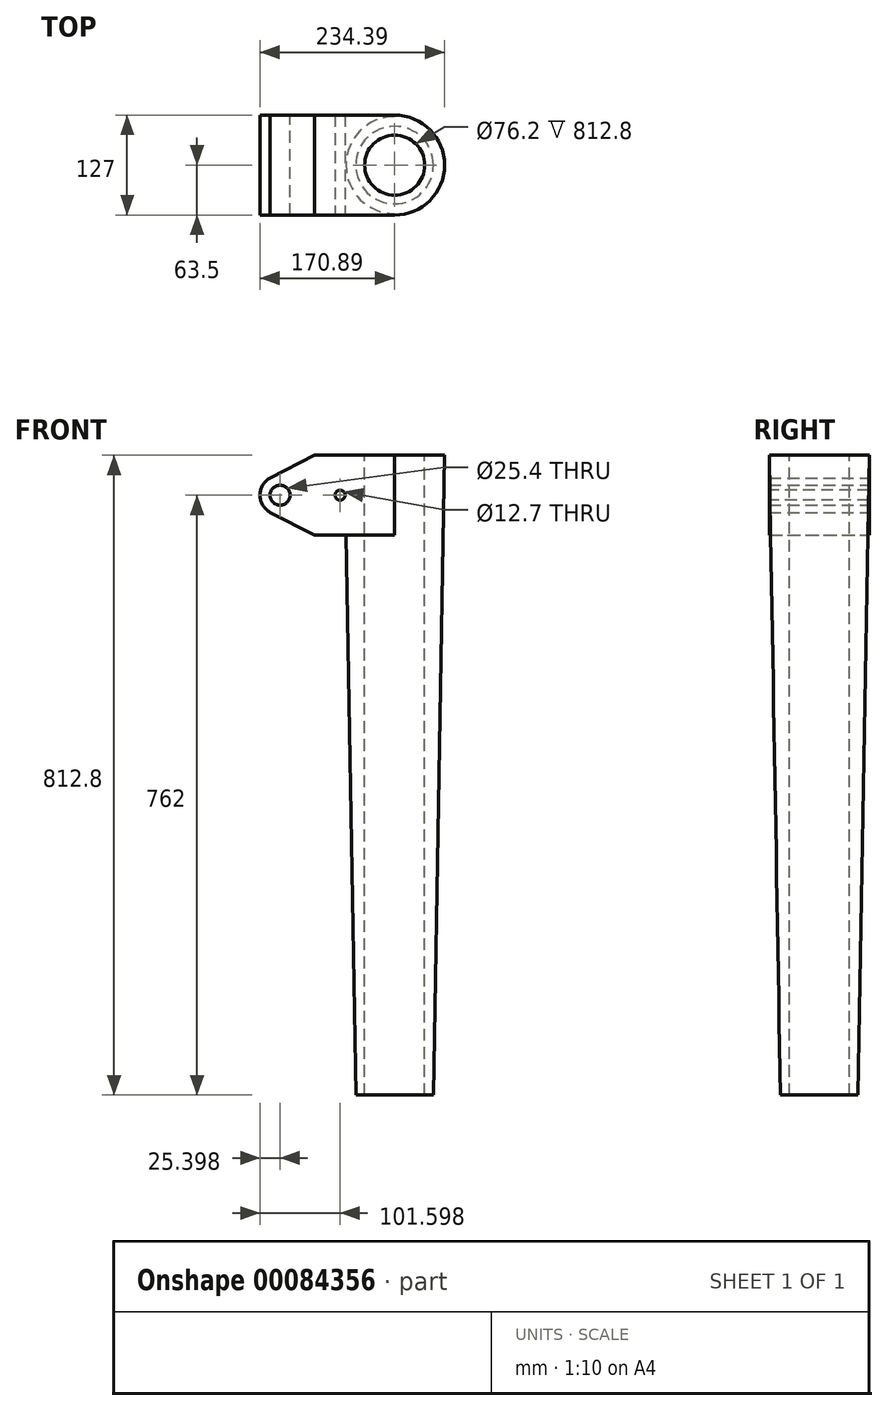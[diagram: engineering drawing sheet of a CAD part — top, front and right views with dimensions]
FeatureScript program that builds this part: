
annotation { "Feature Type Name" : "Feature", "Feature Type Description" : "" }
export const myFeature = defineFeature(function(context is Context, id is Id, definition is map)
    precondition{}
    {
        {
            var Q0;
            Q0=qCreatedBy(makeId("Front.planeOp"),FACE);
            var sketch = newSketch(context, id + "F0", { "sketchPlane" : qUnion([Q0])});
            skLineSegment(sketch, "E0.bottom", {"start": v(0, 0) * mm, "end": v(-101.6, 0) * mm});
            skLineSegment(sketch, "E0.top", {"start": v(0, 101.6) * mm, "end": v(-101.6, 101.6) * mm});
            skLineSegment(sketch, "E0.left", {"start": v(0, 0) * mm, "end": v(0, 101.6) * mm});
            skLineSegment(sketch, "E0.right", {"start": v(-101.6, 0) * mm, "end": v(-101.6, 101.6) * mm});
            skCircle(sketch, "E1", {"center": v(-145.5, 50.8) * mm, "radius": 12.7 * mm});
            skLineSegment(sketch, "E2", {"start": v(0, 50.8) * mm, "end": v(-213.64, 50.8) * mm, "construction": true});
            skArc(sketch, "E3", {"start": v(-158.2, 72.8) * mm, "mid": v(-170.9, 50.8) * mm, "end": v(-158.2, 28.8) * mm});
            skLineSegment(sketch, "E4", {"start": v(-158.2, 72.8) * mm, "end": v(-101.6, 101.6) * mm});
            skLineSegment(sketch, "E5", {"start": v(-158.2, 28.8) * mm, "end": v(-101.6, 0) * mm});
            skLineSegment(sketch, "E6", {"start": v(-158.2, 72.8) * mm, "end": v(-158.2, 28.8) * mm, "construction": true});
            skSolve(sketch);
        }
        {
            var Q0;
            Q0=makeQuery(id+"F0.imprint","IMPRINT",FACE,{"disambiguationData":[TD([[makeQuery(id+"F0.imprint","IMPRINT",EDGE,{"derivedFrom":sQuery(id+"F0.wireOp",EDGE,"E0.bottom")}),-1.0]])]});
            var Q1;
            Q1=makeQuery(id+"F0.imprint","IMPRINT",FACE,{"disambiguationData":[TD([[makeQuery(id+"F0.imprint","IMPRINT",EDGE,{"derivedFrom":sQuery(id+"F0.wireOp",EDGE,"E0.right")}),1.0]])]});
            extrude(context, id + "F1", {"entities" : qUnion([Q0, Q1]), "endBound" : BoundingType.SYMMETRIC, "depth" : 127 * mm});
        }
        {
            var Q0;
            Q0=makeQuery(id+"F1.opExtrude","SWEPT_FACE",FACE,{"disambiguationData":[OSD([sQuery(id+"F0.wireOp",EDGE,"E0.top")])]});
            var sketch = newSketch(context, id + "F2", { "sketchPlane" : qUnion([Q0])});
            skLineSegment(sketch, "E7.0", {"start": v(0, -63.5) * mm, "end": v(0, 63.5) * mm});
            skLineSegment(sketch, "E7.1", {"start": v(0, 63.5) * mm, "end": v(-101.6, 63.5) * mm});
            skLineSegment(sketch, "E7.2", {"start": v(0, -63.5) * mm, "end": v(-101.6, -63.5) * mm});
            skCircle(sketch, "E8", {"center": v(0, 0) * mm, "radius": 63.5 * mm});
            skSolve(sketch);
        }
        {
            var Q0;
            {var subQ0=sQuery(id+"F2.wireOp",EDGE,"E7.0");Q0=makeQuery(id+"F2.imprint","IMPRINT",FACE,{"disambiguationData":[TD([[makeQuery(id+"F2.imprint","IMPRINT",EDGE,{"derivedFrom":subQ0}),1.0]])]});}
            var Q1;
            {var subQ0=sQuery(id+"F2.wireOp",EDGE,"E7.0");Q1=makeQuery(id+"F2.imprint","IMPRINT",FACE,{"disambiguationData":[TD([[makeQuery(id+"F2.imprint","IMPRINT",EDGE,{"derivedFrom":subQ0}),-1.0]])]});}
            extrude(context, id + "F3", {"entities" : qUnion([Q0, Q1]), "operationType" : NewBodyOperationType.ADD, "oppositeDirection" : true, "depth" : 812.8 * mm, "hasDraft" : true, "draftAngle" : 1 * degree, "draftPullDirection" : true});
        }
        {
            var Q0;
            Q0=makeQuery(id+"F3.boolean.opBoolean","MERGE",FACE,{"derivedFrom":[makeQuery(id+"F1.opExtrude","SWEPT_FACE",FACE,{"disambiguationData":[OSD([sQuery(id+"F0.wireOp",EDGE,"E0.top")])]}),makeQuery(id+"F3.opExtrude","CAP_FACE",FACE,{"disambiguationData":[OSD([sQuery(id+"F2.wireOp",EDGE,"E8")])],"isStart":true})]});
            var sketch = newSketch(context, id + "F4", { "sketchPlane" : qUnion([Q0])});
            skArc(sketch, "E9.0", {"start": v(0, -63.5) * mm, "mid": v(63.5, 0) * mm, "end": v(0, 63.5) * mm});
            skLineSegment(sketch, "E9.1", {"start": v(0, 63.5) * mm, "end": v(-101.6, 63.5) * mm});
            skLineSegment(sketch, "E9.2", {"start": v(0, -63.5) * mm, "end": v(-101.6, -63.5) * mm});
            skCircle(sketch, "E10", {"center": v(0, 0) * mm, "radius": 38.1 * mm});
            skSolve(sketch);
        }
        {
            var Q0;
            Q0=makeQuery(id+"F4.imprint","IMPRINT",FACE,{"disambiguationData":[TD([[makeQuery(id+"F4.imprint","IMPRINT",EDGE,{"derivedFrom":sQuery(id+"F4.wireOp",EDGE,"E10")}),1.0]])]});
            extrude(context, id + "F5", {"entities" : qUnion([Q0]), "operationType" : NewBodyOperationType.REMOVE, "endBound" : BoundingType.THROUGH_ALL, "oppositeDirection" : true, "depth" : 25.4 * mm});
        }
        {
            var Q0;
            Q0=makeQuery(id+"F1.opExtrude","CAP_FACE",FACE,{"disambiguationData":[OSD([sQuery(id+"F0.wireOp",EDGE,"E0.bottom"),sQuery(id+"F0.wireOp",EDGE,"E0.top"),sQuery(id+"F0.wireOp",EDGE,"E0.left"),sQuery(id+"F0.wireOp",EDGE,"E1"),sQuery(id+"F0.wireOp",EDGE,"E3"),sQuery(id+"F0.wireOp",EDGE,"E4"),sQuery(id+"F0.wireOp",EDGE,"E5")])],"isStart":false});
            var sketch = newSketch(context, id + "F6", { "sketchPlane" : qUnion([Q0])});
            skCircle(sketch, "E11.0", {"center": v(-145.5, 50.8) * mm, "radius": 12.7 * mm});
            skLineSegment(sketch, "E11.1", {"start": v(-158.2, 72.8) * mm, "end": v(-101.6, 101.6) * mm});
            skLineSegment(sketch, "E11.2", {"start": v(0, 101.6) * mm, "end": v(-101.6, 101.6) * mm});
            skLineSegment(sketch, "E11.3", {"start": v(0, 0) * mm, "end": v(0, 101.6) * mm});
            skLineSegment(sketch, "E11.4", {"start": v(0, 0) * mm, "end": v(-101.6, 0) * mm});
            skLineSegment(sketch, "E11.5", {"start": v(-158.2, 28.8) * mm, "end": v(-101.6, 0) * mm});
            skArc(sketch, "E11.6", {"start": v(-158.2, 72.8) * mm, "mid": v(-170.9, 50.8) * mm, "end": v(-158.2, 28.8) * mm});
            skCircle(sketch, "E12", {"center": v(-69.3, 50.8) * mm, "radius": 6.35 * mm});
            skSolve(sketch);
        }
        {
            var Q0;
            Q0=makeQuery(id+"F6.imprint","IMPRINT",FACE,{"disambiguationData":[TD([[makeQuery(id+"F6.imprint","IMPRINT",EDGE,{"derivedFrom":sQuery(id+"F6.wireOp",EDGE,"E12")}),1.0]])]});
            extrude(context, id + "F7", {"entities" : qUnion([Q0]), "operationType" : NewBodyOperationType.REMOVE, "endBound" : BoundingType.THROUGH_ALL, "oppositeDirection" : true, "depth" : 25.4 * mm});
        }
    });
